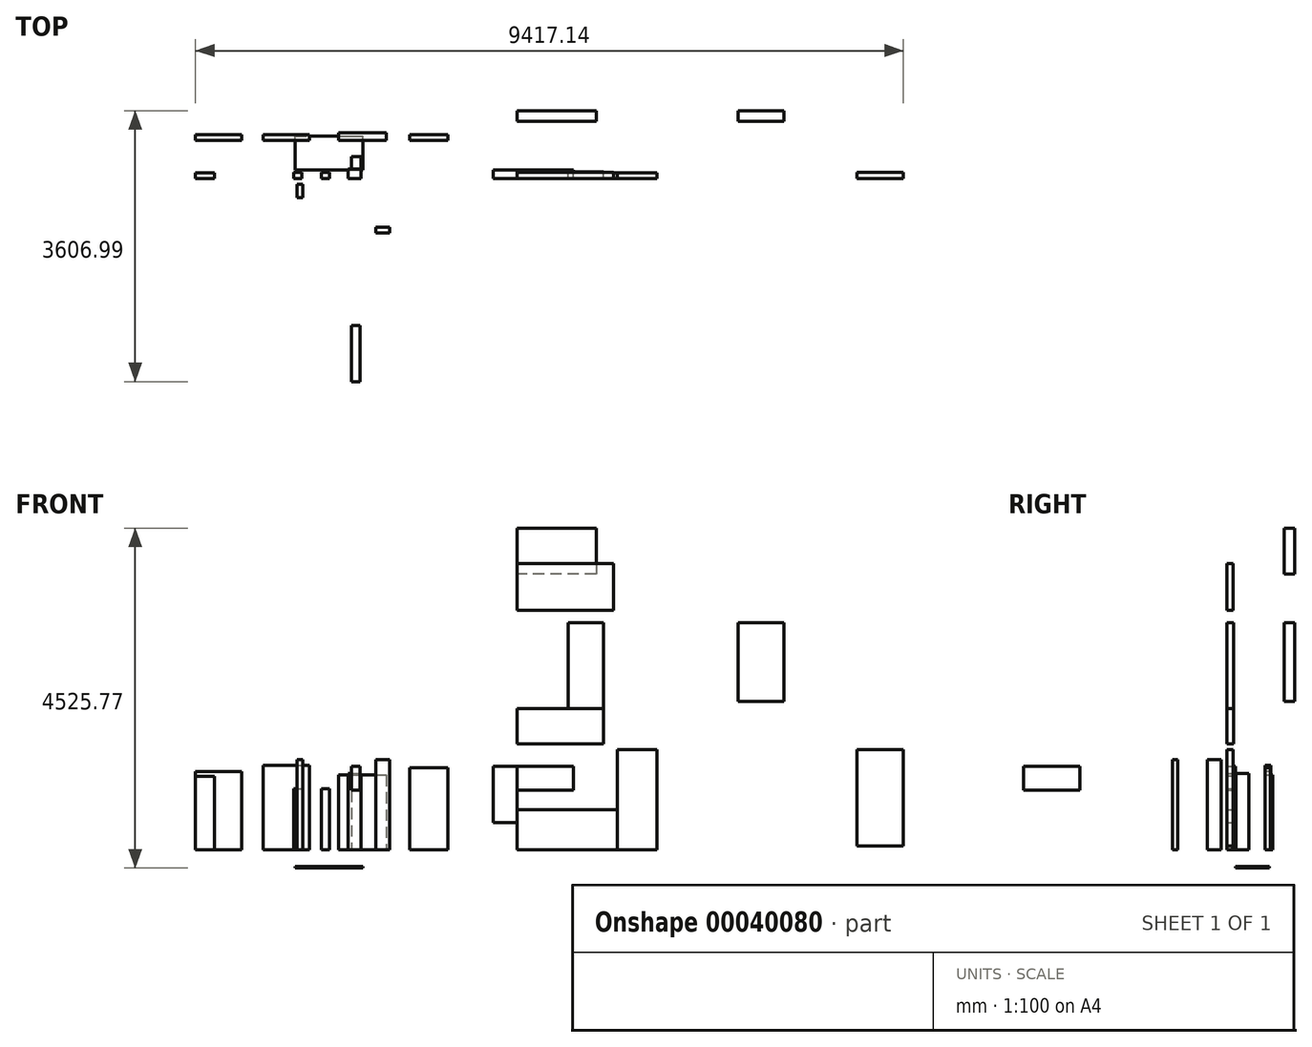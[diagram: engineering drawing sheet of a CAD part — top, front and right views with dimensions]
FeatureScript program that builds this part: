
annotation { "Feature Type Name" : "Feature", "Feature Type Description" : "" }
export const myFeature = defineFeature(function(context is Context, id is Id, definition is map)
    precondition{}
    {
        {
            var Q0;
            Q0=qCreatedBy(makeId("Top.planeOp"),FACE);
            var sketch = newSketch(context, id + "F0", { "sketchPlane" : qUnion([Q0])});
            skLineSegment(sketch, "E0.bottom", {"start": v(-126.82, 23.64) * mm, "end": v(488.18, 23.64) * mm});
            skLineSegment(sketch, "E0.top", {"start": v(-126.82, -56.36) * mm, "end": v(488.18, -56.36) * mm});
            skLineSegment(sketch, "E0.left", {"start": v(-126.82, 23.64) * mm, "end": v(-126.82, -56.36) * mm});
            skLineSegment(sketch, "E0.right", {"start": v(488.18, 23.64) * mm, "end": v(488.18, -56.36) * mm});
            skLineSegment(sketch, "E1.bottom", {"start": v(776.36, -56.36) * mm, "end": v(1391.36, -56.36) * mm});
            skLineSegment(sketch, "E1.top", {"start": v(776.36, 23.64) * mm, "end": v(1391.36, 23.64) * mm});
            skLineSegment(sketch, "E1.left", {"start": v(776.36, -56.36) * mm, "end": v(776.36, 23.64) * mm});
            skLineSegment(sketch, "E1.right", {"start": v(1391.36, -56.36) * mm, "end": v(1391.36, 23.64) * mm});
            skLineSegment(sketch, "E2.bottom", {"start": v(1775.06, -56.36) * mm, "end": v(2410.06, -56.36) * mm});
            skLineSegment(sketch, "E2.top", {"start": v(1775.06, 46.64) * mm, "end": v(2410.06, 46.64) * mm});
            skLineSegment(sketch, "E2.left", {"start": v(1775.06, -56.36) * mm, "end": v(1775.06, 46.64) * mm});
            skLineSegment(sketch, "E2.right", {"start": v(2410.06, -56.36) * mm, "end": v(2410.06, 46.64) * mm});
            skLineSegment(sketch, "E3.bottom", {"start": v(2722.05, -56.36) * mm, "end": v(3232.05, -56.36) * mm});
            skLineSegment(sketch, "E3.top", {"start": v(2722.05, 18.64) * mm, "end": v(3232.05, 18.64) * mm});
            skLineSegment(sketch, "E3.left", {"start": v(2722.05, -56.36) * mm, "end": v(2722.05, 18.64) * mm});
            skLineSegment(sketch, "E3.right", {"start": v(3232.05, -56.36) * mm, "end": v(3232.05, 18.64) * mm});
            skLineSegment(sketch, "E4.bottom", {"start": v(-126.82, -488.47) * mm, "end": v(128.18, -488.47) * mm});
            skLineSegment(sketch, "E4.top", {"start": v(-126.82, -563.47) * mm, "end": v(128.18, -563.47) * mm});
            skLineSegment(sketch, "E4.left", {"start": v(-126.82, -488.47) * mm, "end": v(-126.82, -563.47) * mm});
            skLineSegment(sketch, "E4.right", {"start": v(128.18, -488.47) * mm, "end": v(128.18, -563.47) * mm});
            skLineSegment(sketch, "E5.bottom", {"start": v(346.92, -563.47) * mm, "end": v(966.92, -563.47) * mm});
            skLineSegment(sketch, "E5.top", {"start": v(346.92, -478.47) * mm, "end": v(966.92, -478.47) * mm});
            skLineSegment(sketch, "E5.left", {"start": v(346.92, -563.47) * mm, "end": v(346.92, -478.47) * mm});
            skLineSegment(sketch, "E5.right", {"start": v(966.92, -563.47) * mm, "end": v(966.92, -478.47) * mm});
            skLineSegment(sketch, "E6.bottom", {"start": v(1181.05, -563.47) * mm, "end": v(1291.05, -563.47) * mm});
            skLineSegment(sketch, "E6.top", {"start": v(1181.05, -478.47) * mm, "end": v(1291.05, -478.47) * mm});
            skLineSegment(sketch, "E6.left", {"start": v(1181.05, -563.47) * mm, "end": v(1181.05, -478.47) * mm});
            skLineSegment(sketch, "E6.right", {"start": v(1291.05, -563.47) * mm, "end": v(1291.05, -478.47) * mm});
            skLineSegment(sketch, "E7.bottom", {"start": v(1547.08, -563.47) * mm, "end": v(1657.08, -563.47) * mm});
            skLineSegment(sketch, "E7.top", {"start": v(1547.08, -478.47) * mm, "end": v(1657.08, -478.47) * mm});
            skLineSegment(sketch, "E7.left", {"start": v(1547.08, -563.47) * mm, "end": v(1547.08, -478.47) * mm});
            skLineSegment(sketch, "E7.right", {"start": v(1657.08, -563.47) * mm, "end": v(1657.08, -478.47) * mm});
            skLineSegment(sketch, "E8.bottom", {"start": v(1906.08, -563.47) * mm, "end": v(2076.08, -563.47) * mm});
            skLineSegment(sketch, "E8.top", {"start": v(1906.08, -438.47) * mm, "end": v(2076.08, -438.47) * mm});
            skLineSegment(sketch, "E8.left", {"start": v(1906.08, -563.47) * mm, "end": v(1906.08, -438.47) * mm});
            skLineSegment(sketch, "E8.right", {"start": v(2076.08, -563.47) * mm, "end": v(2076.08, -438.47) * mm});
            skLineSegment(sketch, "E9.bottom", {"start": v(2275.63, -563.47) * mm, "end": v(2745.63, -563.47) * mm});
            skLineSegment(sketch, "E9.top", {"start": v(2275.63, -473.47) * mm, "end": v(2745.63, -473.47) * mm});
            skLineSegment(sketch, "E9.left", {"start": v(2275.63, -563.47) * mm, "end": v(2275.63, -473.47) * mm});
            skLineSegment(sketch, "E9.right", {"start": v(2745.63, -563.47) * mm, "end": v(2745.63, -473.47) * mm});
            skLineSegment(sketch, "E10.bottom", {"start": v(3042.9, -563.47) * mm, "end": v(3362.9, -563.47) * mm});
            skLineSegment(sketch, "E10.top", {"start": v(3042.9, -448.47) * mm, "end": v(3362.9, -448.47) * mm});
            skLineSegment(sketch, "E10.left", {"start": v(3042.9, -563.47) * mm, "end": v(3042.9, -448.47) * mm});
            skLineSegment(sketch, "E10.right", {"start": v(3362.9, -563.47) * mm, "end": v(3362.9, -448.47) * mm});
            skLineSegment(sketch, "E11.bottom", {"start": v(3623.62, -563.47) * mm, "end": v(4153.62, -563.47) * mm});
            skLineSegment(sketch, "E11.top", {"start": v(3623.62, -485.47) * mm, "end": v(4153.62, -485.47) * mm});
            skLineSegment(sketch, "E11.left", {"start": v(3623.62, -563.47) * mm, "end": v(3623.62, -485.47) * mm});
            skLineSegment(sketch, "E11.right", {"start": v(4153.62, -563.47) * mm, "end": v(4153.62, -485.47) * mm});
            skLineSegment(sketch, "E12.bottom", {"start": v(2275.63, -1213) * mm, "end": v(2457.63, -1213) * mm});
            skLineSegment(sketch, "E12.top", {"start": v(2275.63, -1288) * mm, "end": v(2457.63, -1288) * mm});
            skLineSegment(sketch, "E12.left", {"start": v(2275.63, -1213) * mm, "end": v(2275.63, -1288) * mm});
            skLineSegment(sketch, "E12.right", {"start": v(2457.63, -1213) * mm, "end": v(2457.63, -1288) * mm});
            skLineSegment(sketch, "E13.bottom", {"start": v(-126.82, 200.98) * mm, "end": v(483.18, 200.98) * mm});
            skLineSegment(sketch, "E13.top", {"start": v(-126.82, 340.98) * mm, "end": v(483.18, 340.98) * mm});
            skLineSegment(sketch, "E13.left", {"start": v(-126.82, 200.98) * mm, "end": v(-126.82, 340.98) * mm});
            skLineSegment(sketch, "E13.right", {"start": v(483.18, 200.98) * mm, "end": v(483.18, 340.98) * mm});
            skSolve(sketch);
        }
        {
            var Q0;
            Q0=makeQuery(id+"F0.imprint","IMPRINT",FACE,{"disambiguationData":[TD([[makeQuery(id+"F0.imprint","IMPRINT",EDGE,{"derivedFrom":sQuery(id+"F0.wireOp",EDGE,"E0.bottom")}),-1.0]])]});
            extrude(context, id + "F1", {"entities" : qUnion([Q0]), "depth" : 1040 * mm});
        }
        {
            var Q0;
            Q0=makeQuery(id+"F0.imprint","IMPRINT",FACE,{"disambiguationData":[TD([[makeQuery(id+"F0.imprint","IMPRINT",EDGE,{"derivedFrom":sQuery(id+"F0.wireOp",EDGE,"E1.bottom")}),1.0]])]});
            extrude(context, id + "F2", {"entities" : qUnion([Q0]), "depth" : 1120 * mm});
        }
        {
            var Q0;
            Q0=makeQuery(id+"F0.imprint","IMPRINT",FACE,{"disambiguationData":[TD([[makeQuery(id+"F0.imprint","IMPRINT",EDGE,{"derivedFrom":sQuery(id+"F0.wireOp",EDGE,"E2.bottom")}),1.0]])]});
            extrude(context, id + "F3", {"entities" : qUnion([Q0]), "depth" : 995 * mm});
        }
        {
            var Q0;
            Q0=makeQuery(id+"F0.imprint","IMPRINT",FACE,{"disambiguationData":[TD([[makeQuery(id+"F0.imprint","IMPRINT",EDGE,{"derivedFrom":sQuery(id+"F0.wireOp",EDGE,"E3.bottom")}),1.0]])]});
            extrude(context, id + "F4", {"entities" : qUnion([Q0]), "depth" : 1090 * mm});
        }
        {
            var Q0;
            Q0=makeQuery(id+"F0.imprint","IMPRINT",FACE,{"disambiguationData":[TD([[makeQuery(id+"F0.imprint","IMPRINT",EDGE,{"derivedFrom":sQuery(id+"F0.wireOp",EDGE,"E4.bottom")}),-1.0]])]});
            extrude(context, id + "F5", {"entities" : qUnion([Q0]), "depth" : 975 * mm});
        }
        {
            var Q0;
            Q0=makeQuery(id+"F0.imprint","IMPRINT",FACE,{"disambiguationData":[TD([[makeQuery(id+"F0.imprint","IMPRINT",EDGE,{"derivedFrom":sQuery(id+"F0.wireOp",EDGE,"E5.bottom")}),1.0]])]});
            extrude(context, id + "F6", {"entities" : qUnion([Q0]), "depth" : 1280 * mm});
        }
        {
            var Q0;
            Q0=makeQuery(id+"F0.imprint","IMPRINT",FACE,{"disambiguationData":[TD([[makeQuery(id+"F0.imprint","IMPRINT",EDGE,{"derivedFrom":sQuery(id+"F0.wireOp",EDGE,"E6.bottom")}),1.0]])]});
            extrude(context, id + "F7", {"entities" : qUnion([Q0]), "depth" : 810 * mm});
        }
        {
            var Q0;
            Q0=makeQuery(id+"F0.imprint","IMPRINT",FACE,{"disambiguationData":[TD([[makeQuery(id+"F0.imprint","IMPRINT",EDGE,{"derivedFrom":sQuery(id+"F0.wireOp",EDGE,"E7.bottom")}),1.0]])]});
            extrude(context, id + "F8", {"entities" : qUnion([Q0]), "depth" : 810 * mm});
        }
        {
            var Q0;
            Q0=makeQuery(id+"F0.imprint","IMPRINT",FACE,{"disambiguationData":[TD([[makeQuery(id+"F0.imprint","IMPRINT",EDGE,{"derivedFrom":sQuery(id+"F0.wireOp",EDGE,"E8.bottom")}),1.0]])]});
            extrude(context, id + "F9", {"entities" : qUnion([Q0]), "depth" : 1015 * mm});
        }
        {
            var Q0;
            Q0=makeQuery(id+"F0.imprint","IMPRINT",FACE,{"disambiguationData":[TD([[makeQuery(id+"F0.imprint","IMPRINT",EDGE,{"derivedFrom":sQuery(id+"F0.wireOp",EDGE,"E9.bottom")}),1.0]])]});
            extrude(context, id + "F10", {"entities" : qUnion([Q0]), "depth" : 1145 * mm});
        }
        {
            var Q0;
            Q0=makeQuery(id+"F0.imprint","IMPRINT",FACE,{"disambiguationData":[TD([[makeQuery(id+"F0.imprint","IMPRINT",EDGE,{"derivedFrom":sQuery(id+"F0.wireOp",EDGE,"E10.bottom")}),1.0]])]});
            extrude(context, id + "F11", {"entities" : qUnion([Q0]), "depth" : 750 * mm});
        }
        {
            var Q0;
            Q0=makeQuery(id+"F0.imprint","IMPRINT",FACE,{"disambiguationData":[TD([[makeQuery(id+"F0.imprint","IMPRINT",EDGE,{"derivedFrom":sQuery(id+"F0.wireOp",EDGE,"E11.bottom")}),1.0]])]});
            extrude(context, id + "F12", {"entities" : qUnion([Q0]), "depth" : 1330 * mm});
        }
        {
            var Q0;
            Q0=makeQuery(id+"F0.imprint","IMPRINT",FACE,{"disambiguationData":[TD([[makeQuery(id+"F0.imprint","IMPRINT",EDGE,{"derivedFrom":sQuery(id+"F0.wireOp",EDGE,"E12.bottom")}),-1.0]])]});
            extrude(context, id + "F13", {"entities" : qUnion([Q0]), "depth" : 1200 * mm});
        }
        {
            var Q0;
            Q0=qCreatedBy(makeId("Front.planeOp"),FACE);
            var sketch = newSketch(context, id + "F14", { "sketchPlane" : qUnion([Q0])});
            skLineSegment(sketch, "E14.bottom", {"start": v(1199.49, -220.33) * mm, "end": v(2099.49, -220.33) * mm});
            skLineSegment(sketch, "E14.top", {"start": v(1199.49, -245.33) * mm, "end": v(2099.49, -245.33) * mm});
            skLineSegment(sketch, "E14.left", {"start": v(1199.49, -220.33) * mm, "end": v(1199.49, -245.33) * mm});
            skLineSegment(sketch, "E14.right", {"start": v(2099.49, -220.33) * mm, "end": v(2099.49, -245.33) * mm});
            skSolve(sketch);
        }
        {
            var Q0;
            Q0=makeQuery(id+"F14.imprint","IMPRINT",FACE,{"disambiguationData":[TD([[makeQuery(id+"F14.imprint","IMPRINT",EDGE,{"derivedFrom":sQuery(id+"F14.wireOp",EDGE,"E14.bottom")}),-1.0]])]});
            extrude(context, id + "F15", {"entities" : qUnion([Q0]), "depth" : 450 * mm});
        }
        {
            var Q0;
            Q0=makeQuery(id+"F0.imprint","IMPRINT",FACE,{"disambiguationData":[TD([[makeQuery(id+"F0.imprint","IMPRINT",EDGE,{"derivedFrom":sQuery(id+"F0.wireOp",EDGE,"E13.bottom")}),1.0]])]});
            extrude(context, id + "F16", {"entities" : qUnion([Q0]), "depth" : 1050 * mm});
        }
        {
            var Q0;
            Q0=makeQuery(id+"F6.opExtrude","SWEPT_BODY",BODY,{"disambiguationData":[OSD([sQuery(id+"F0.wireOp",EDGE,"E5.bottom"),sQuery(id+"F0.wireOp",EDGE,"E5.top"),sQuery(id+"F0.wireOp",EDGE,"E5.left"),sQuery(id+"F0.wireOp",EDGE,"E5.right")])]});
            var Q1;
            Q1=makeQuery(id+"F12.opExtrude","SWEPT_BODY",BODY,{"disambiguationData":[OSD([sQuery(id+"F0.wireOp",EDGE,"E11.bottom"),sQuery(id+"F0.wireOp",EDGE,"E11.top"),sQuery(id+"F0.wireOp",EDGE,"E11.left"),sQuery(id+"F0.wireOp",EDGE,"E11.right")])]});
            var Q2;
            Q2=makeQuery(id+"F10.opExtrude","SWEPT_BODY",BODY,{"disambiguationData":[OSD([sQuery(id+"F0.wireOp",EDGE,"E9.bottom"),sQuery(id+"F0.wireOp",EDGE,"E9.top"),sQuery(id+"F0.wireOp",EDGE,"E9.left"),sQuery(id+"F0.wireOp",EDGE,"E9.right")])]});
            var Q3;
            Q3=makeQuery(id+"F16.opExtrude","SWEPT_BODY",BODY,{"disambiguationData":[OSD([sQuery(id+"F0.wireOp",EDGE,"E13.bottom"),sQuery(id+"F0.wireOp",EDGE,"E13.top"),sQuery(id+"F0.wireOp",EDGE,"E13.left"),sQuery(id+"F0.wireOp",EDGE,"E13.right")])]});
            var Q4;
            Q4=makeQuery(id+"F11.opExtrude","SWEPT_BODY",BODY,{"disambiguationData":[OSD([sQuery(id+"F0.wireOp",EDGE,"E10.bottom"),sQuery(id+"F0.wireOp",EDGE,"E10.top"),sQuery(id+"F0.wireOp",EDGE,"E10.left"),sQuery(id+"F0.wireOp",EDGE,"E10.right")])]});
            var Q5;
            Q5=makeQuery(id+"F12.opExtrude","CAP_EDGE",EDGE,{"disambiguationData":[OSD([sQuery(id+"F0.wireOp",EDGE,"E11.right")])],"isStart":true});
            transform(context, id + "F17", {"entities" : qUnion([Q0, Q1, Q2, Q3, Q4]), "transformType" : TransformType.ROTATION, "transformAxis" : qUnion([Q5]), "angle" : 90 * degree, "makeCopy" : false});
        }
        {
            var Q0;
            Q0=makeQuery(id+"F13.opExtrude","SWEPT_BODY",BODY,{"disambiguationData":[OSD([sQuery(id+"F0.wireOp",EDGE,"E12.bottom"),sQuery(id+"F0.wireOp",EDGE,"E12.top"),sQuery(id+"F0.wireOp",EDGE,"E12.left"),sQuery(id+"F0.wireOp",EDGE,"E12.right")])]});
            var Q1;
            Q1=makeQuery(id+"F11.opExtrude","SWEPT_BODY",BODY,{"disambiguationData":[OSD([sQuery(id+"F0.wireOp",EDGE,"E10.bottom"),sQuery(id+"F0.wireOp",EDGE,"E10.top"),sQuery(id+"F0.wireOp",EDGE,"E10.left"),sQuery(id+"F0.wireOp",EDGE,"E10.right")])]});
            var Q2;
            Q2=makeQuery(id+"F9.opExtrude","SWEPT_BODY",BODY,{"disambiguationData":[OSD([sQuery(id+"F0.wireOp",EDGE,"E8.bottom"),sQuery(id+"F0.wireOp",EDGE,"E8.top"),sQuery(id+"F0.wireOp",EDGE,"E8.left"),sQuery(id+"F0.wireOp",EDGE,"E8.right")])]});
            var Q3;
            Q3=makeQuery(id+"F9.opExtrude","SWEPT_EDGE",EDGE,{"disambiguationData":[OSD([sQuery(id+"F0.wireOp",EDGE,"E8.top"),sQuery(id+"F0.wireOp",EDGE,"E8.right")])]});
            transform(context, id + "F18", {"entities" : qUnion([Q0, Q1, Q2]), "transformType" : TransformType.ROTATION, "transformAxis" : qUnion([Q3]), "angle" : 90 * degree, "makeCopy" : true});
        }
        {
            var Q0;
            Q0=makeQuery(id+"F11.opExtrude","SWEPT_BODY",BODY,{"disambiguationData":[OSD([sQuery(id+"F0.wireOp",EDGE,"E10.bottom"),sQuery(id+"F0.wireOp",EDGE,"E10.top"),sQuery(id+"F0.wireOp",EDGE,"E10.left"),sQuery(id+"F0.wireOp",EDGE,"E10.right")])]});
            var Q1;
            Q1=makeQuery(id+"F11.opExtrude","CAP_EDGE",EDGE,{"disambiguationData":[OSD([sQuery(id+"F0.wireOp",EDGE,"E10.left")])],"isStart":true});
            transform(context, id + "F19", {"entities" : qUnion([Q0]), "transformType" : TransformType.ROTATION, "transformAxis" : qUnion([Q1]), "angle" : 90 * degree, "makeCopy" : true});
        }
        {
            var Q0;
            Q0=makeQuery(id+"F10.opExtrude","SWEPT_BODY",BODY,{"disambiguationData":[OSD([sQuery(id+"F0.wireOp",EDGE,"E9.bottom"),sQuery(id+"F0.wireOp",EDGE,"E9.top"),sQuery(id+"F0.wireOp",EDGE,"E9.left"),sQuery(id+"F0.wireOp",EDGE,"E9.right")])]});
            var Q1;
            Q1=makeQuery(id+"F16.opExtrude","SWEPT_BODY",BODY,{"disambiguationData":[OSD([sQuery(id+"F0.wireOp",EDGE,"E13.bottom"),sQuery(id+"F0.wireOp",EDGE,"E13.top"),sQuery(id+"F0.wireOp",EDGE,"E13.left"),sQuery(id+"F0.wireOp",EDGE,"E13.right")])]});
            var Q2;
            Q2=makeQuery(id+"F10.opExtrude","CAP_EDGE",EDGE,{"disambiguationData":[OSD([sQuery(id+"F0.wireOp",EDGE,"E9.left")])],"isStart":false});
            transform(context, id + "F20", {"entities" : qUnion([Q0, Q1]), "transformType" : TransformType.ROTATION, "transformAxis" : qUnion([Q2]), "angle" : 90 * degree, "makeCopy" : true});
        }
        {
            var Q0;
            Q0=makeQuery(id+"F12.opExtrude","SWEPT_BODY",BODY,{"disambiguationData":[OSD([sQuery(id+"F0.wireOp",EDGE,"E11.bottom"),sQuery(id+"F0.wireOp",EDGE,"E11.top"),sQuery(id+"F0.wireOp",EDGE,"E11.left"),sQuery(id+"F0.wireOp",EDGE,"E11.right")])]});
            var Q1;
            Q1=makeQuery(id+"F6.opExtrude","SWEPT_BODY",BODY,{"disambiguationData":[OSD([sQuery(id+"F0.wireOp",EDGE,"E5.bottom"),sQuery(id+"F0.wireOp",EDGE,"E5.top"),sQuery(id+"F0.wireOp",EDGE,"E5.left"),sQuery(id+"F0.wireOp",EDGE,"E5.right")])]});
            var Q2;
            Q2=makeQuery(id+"F12.opExtrude","CAP_EDGE",EDGE,{"disambiguationData":[OSD([sQuery(id+"F0.wireOp",EDGE,"E11.right")])],"isStart":false});
            transform(context, id + "F21", {"entities" : qUnion([Q0, Q1]), "transformType" : TransformType.ROTATION, "transformAxis" : qUnion([Q2]), "angle" : 90 * degree, "makeCopy" : true});
        }
    });
